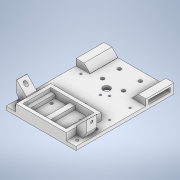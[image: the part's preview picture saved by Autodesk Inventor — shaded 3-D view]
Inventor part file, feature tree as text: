
AUTODESK INVENTOR PART (.ipt)
format: ipt  version: 2022 (Build 260153000, 153)  size: 384,000 bytes
history: native  units: in
note: dims shown in document units (in); Inventor stores cm internally (conversion verified against a paired STEP export)
features: extrude x15, sketch x11, other x4, chamfer x2, mirror x2
ambient origin geometry x8: Origin, YZ Plane, XZ Plane, XY Plane, X Axis, Y Axis, Z Axis, Center Point
bodies: Solid1 (feature_tree)
feature tree (34):
  extrude  "main chassis frame"  Depth=5.0in
  extrude  "mounting holes for caster"  Depth=0.25in TaperAngle=0.0deg
  extrude  "cut in half to mirror holes later"  Depth=1.75in
  extrude  "zip tie mounting holes for motors"  Depth=0.25in
  extrude  "motor mount covers"  Depth=0.25in TaperAngle=0.0deg
  chamfer  "motor mount slants"  Distance=0.45in
  mirror  "Mirror6"
  extrude  "new hole for motor wires"  Depth=0.25in TaperAngle=0.0deg
  extrude  "uno mounting holes"  Depth=0.1875in
  extrude  "L298N mount holes"  Depth=0.14in
  extrude  "battery walls"  Depth=0.25in
  extrude  "battery inner walls"  Depth=0.075in
  extrude  "motor mount slot - R"  Depth=0.5in
  extrude  "side panel mount pillar"  Depth=0.5in
  chamfer  "side panel mount pillar slant"  Distance=1.35in
  other  "side panel mount hole"
  extrude  "side panel mount pillar hole - R"  Depth=0.5in TaperAngle=0.0deg
  extrude  "side panel mount pillar hole rim - R"  Depth=0.05in
  extrude  "side panel mount pillar wire passageway - R"  Depth=0.5in
  mirror  "Mirror7"
  other  "side panel hole dimensions"
  sketch  "Sketch1"  dims[d0=7.0in d1=5.0in]
  sketch  "Sketch4"  dims[d2=0.25in d3=0.0in d19=0.1875in d21=0.25in d22=0.0in]
  sketch  "Sketch5"  dims[d23=0.25in d24=0.0in d26=1.75in]
  sketch  "Sketch6"  dims[d27=0.25in d28=1.2in]
  sketch  "Sketch12"  dims[d29=0.25in d30=0.25in d31=0.0in d80=0.45in d81=0.0in]
  sketch  "Sketch22"  dims[d82=0.4375in d83=0.125in d84=45.0deg d141=0.25in d142=0.0in]
  other  "arduino uno mounting holes"
  other  "motor mount holes sketch"
  sketch  "Sketch32"  dims[d164=1.1775in d165=0.1875in d166=1.1775in]
  sketch  "Sketch33"  dims[d167=0.931in d186=0.14in]
  sketch  "Sketch34"  dims[d189=0.25in d190=0.0in d208=1.7125in]
  sketch  "Sketch36"  dims[d209=1.7125in d210=0.075in]
  sketch  "Sketch38"  dims[d211=0.075in d214=1.35in d215=1.35in d216=1.35in d217=0.2625in d218=0.0in d219=0.05in d220=0.6in d221=1.1in d222=0.2in d223=2.0in d224=0.14in d225=1.55in d226=0.3in d227=2.0in d228=1.0in d229=0.5in d230=0.0in d235=2.5in d236=2.0in d237=3.6in d238=3.1in d239=0.25in d240=0.25in d241=0.25in d242=0.25in d243=0.5in d244=0.0in d245=0.25in d246=0.0in d251=1.25in d252=0.0in d253=0.6875in d254=0.125in d255=45.0deg d256=0.1875in d257=0.25in d258=0.5625in d259=0.0in d260=0.04in d261=0.0in d262=0.7725in d263=0.0in d264=0.75in d265=0.3715in d266=1.1215in d267=5.8785in d268=0.26in d206=0.5in d207=0.0344in]
